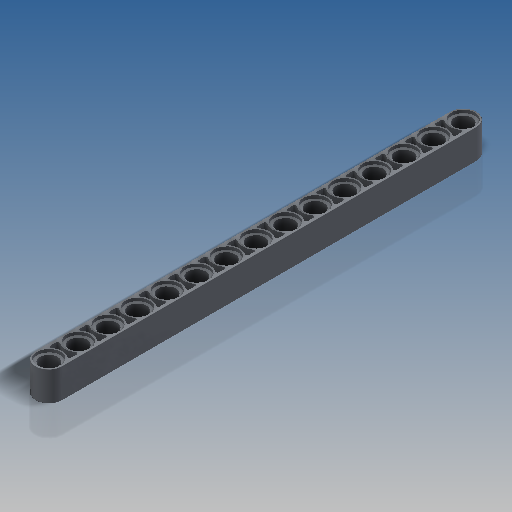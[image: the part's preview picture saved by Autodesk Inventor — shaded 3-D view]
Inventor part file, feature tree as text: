
AUTODESK INVENTOR PART (.ipt)
format: ipt  version: 2019.4 (Build 234330000, 330)  size: 612,864 bytes
history: native  units: mm
features: extrude x3, sketch x2, projected_geometry x2, mirror x1, fillet x1
ambient origin geometry x8: Origin, YZ Plane, XZ Plane, XY Plane, X Axis, Y Axis, Z Axis, Center Point
bodies: Solid1 (feature_tree)
feature tree (9):
  extrude  "Extrusion1"  Depth=7.2mm
  sketch  "Sketch6"  dims[d41=0.8mm d42=0.0mm d43=3.1mm d44=0.0mm d48=112.0mm d49=6.4mm d50=4.8mm d51=8.0mm d52=0.8mm d53=140.0mm d55=8.0mm d56=10.0mm d58=10.0mm d60=0.4mm d61=0.1mm]
  extrude  "Extrusion7"  Depth=3.1mm TaperAngle=0.0deg
  extrude  "Extrusion8"  Depth=0.1mm
  mirror  "Mirror1"
  fillet  "Fillet2"  Radius=6.4mm
  sketch  "Sketch1"  dims[d14=8.0mm d15=0.0mm d32=7.2mm]
  projected_geometry  "Projected Loop3"
  projected_geometry  "Projected Loop4"
